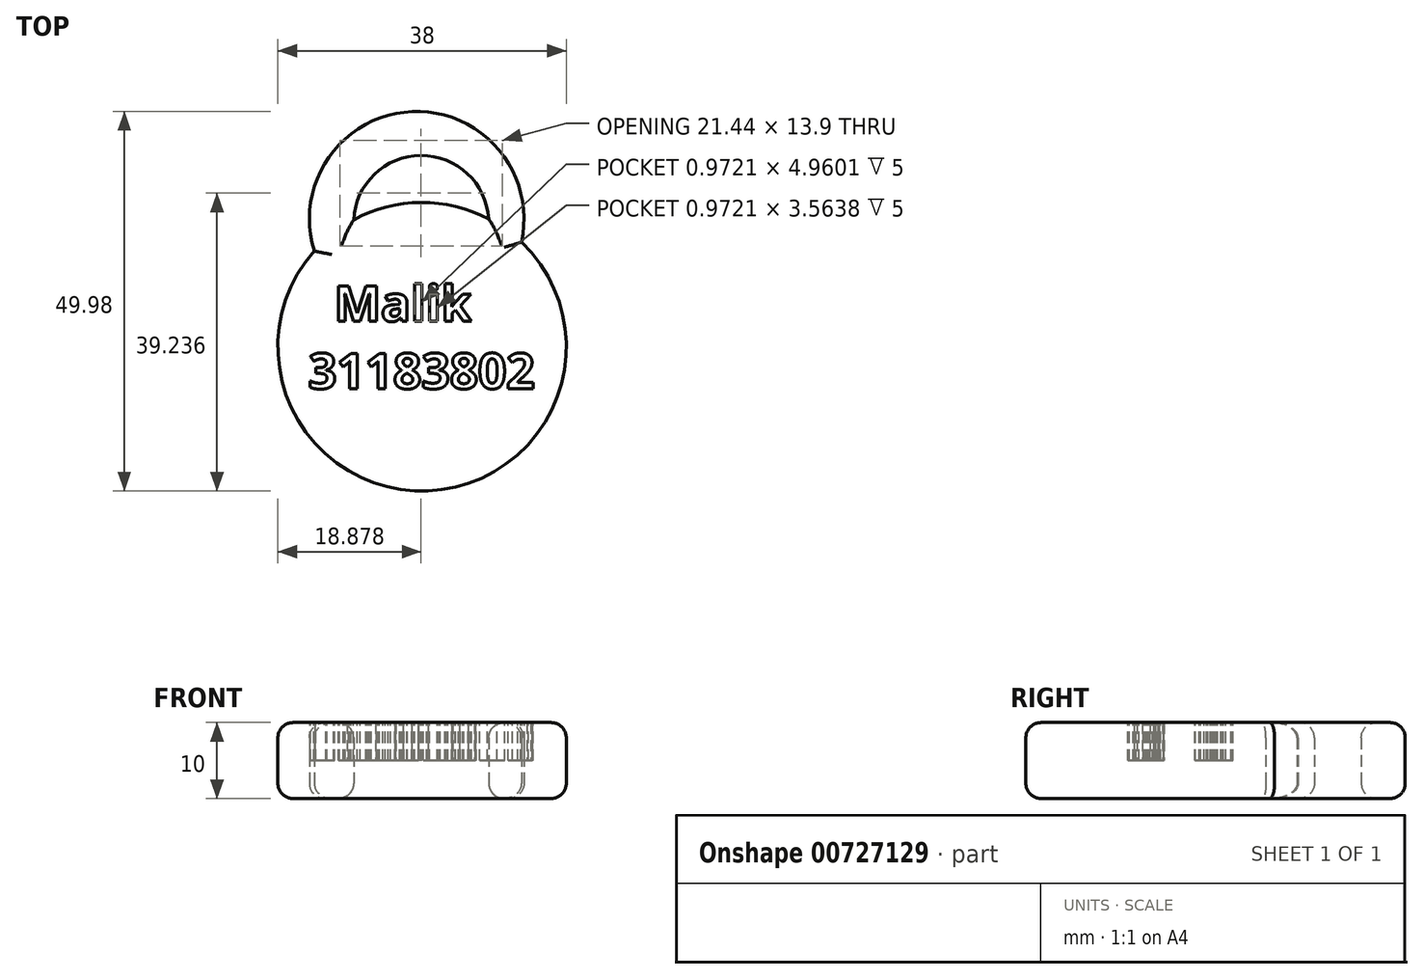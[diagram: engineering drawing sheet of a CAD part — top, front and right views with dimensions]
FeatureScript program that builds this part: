
annotation { "Feature Type Name" : "Feature", "Feature Type Description" : "" }
export const myFeature = defineFeature(function(context is Context, id is Id, definition is map)
    precondition{}
    {
        {
            var Q0;
            Q0=qCreatedBy(makeId("Top.planeOp"),FACE);
            var sketch = newSketch(context, id + "F0", { "sketchPlane" : qUnion([Q0])});
            skCircle(sketch, "E0", {"center": v(0, 0) * mm, "radius": 19 * mm});
            skArc(sketch, "E1", {"start": v(13.1, 13.77) * mm, "mid": v(-1.3, 30.97) * mm, "end": v(-14.2, 12.62) * mm});
            skArc(sketch, "E2", {"start": v(8.8, 16.85) * mm, "mid": v(-0.17, 25.19) * mm, "end": v(-9.01, 16.73) * mm});
            skSolve(sketch);
        }
        {
            var Q0;
            {var subQ0=sQuery(id+"F0.wireOp",EDGE,"E1");var subQ1=sQuery(id+"F0.wireOp",EDGE,"E0");var subQ2=makeQuery(id+"F0.imprint","INTERSECT",VERTEX,{"disambiguationData":[OD(0.0)],"derivedFrom":[subQ1,subQ0]});Q0=makeQuery(id+"F0.imprint","IMPRINT",FACE,{"disambiguationData":[TD([[makeQuery(id+"F0.imprint","IMPRINT",EDGE,{"disambiguationData":[TD([[subQ2,-1.0]])],"derivedFrom":subQ1}),1.0]])]});}
            var Q1;
            {var subQ0=sQuery(id+"F0.wireOp",EDGE,"E1");Q1=makeQuery(id+"F0.imprint","IMPRINT",FACE,{"disambiguationData":[TD([[makeQuery(id+"F0.imprint","IMPRINT",EDGE,{"derivedFrom":subQ0}),1.0]])]});}
            extrude(context, id + "F1", {"entities" : qUnion([Q0, Q1]), "depth" : 10 * mm, "offsetDistance" : 25 * mm});
        }
        {
            var Q0;
            Q0=makeQuery(id+"F1.opExtrude","CAP_FACE",FACE,{"disambiguationData":[OSD([sQuery(id+"F0.wireOp",EDGE,"E0"),sQuery(id+"F0.wireOp",EDGE,"E1"),sQuery(id+"F0.wireOp",EDGE,"E2")])],"isStart":false});
            fillet(context, id + "F2", {"entities" : qUnion([Q0]), "radius" : 2 * mm, "tangentPropagation" : true, "allowEdgeOverflow" : false});
        }
        {
            var Q0;
            Q0=makeQuery(id+"F1.opExtrude","CAP_FACE",FACE,{"disambiguationData":[OSD([sQuery(id+"F0.wireOp",EDGE,"E0"),sQuery(id+"F0.wireOp",EDGE,"E1"),sQuery(id+"F0.wireOp",EDGE,"E2")])],"isStart":true});
            fillet(context, id + "F3", {"entities" : qUnion([Q0]), "radius" : 2 * mm, "tangentPropagation" : true, "allowEdgeOverflow" : false});
        }
        {
            var Q0;
            Q0=makeQuery(id+"F1.opExtrude","CAP_FACE",FACE,{"disambiguationData":[OSD([sQuery(id+"F0.wireOp",EDGE,"E0"),sQuery(id+"F0.wireOp",EDGE,"E1"),sQuery(id+"F0.wireOp",EDGE,"E2")])],"isStart":false});
            var sketch = newSketch(context, id + "F4", { "sketchPlane" : qUnion([Q0])});
            skText(sketch, "E3", { "text": "  Malik\n31183802", "fontName": "OpenSans-Bold.ttf"});
            const initialGuessF4  = {"E3": [-0.01498, 0.00335, 1, 0, 0.0047]};
            skSetInitialGuess(sketch, initialGuessF4);
            skSolve(sketch);
        }
        {
            var Q0;
            Q0 = qSketchRegion(id + "F4", true);
            extrude(context, id + "F5", {"entities" : qUnion([Q0]), "operationType" : NewBodyOperationType.REMOVE, "oppositeDirection" : true, "depth" : 5 * mm, "offsetDistance" : 25 * mm});
        }
    });
